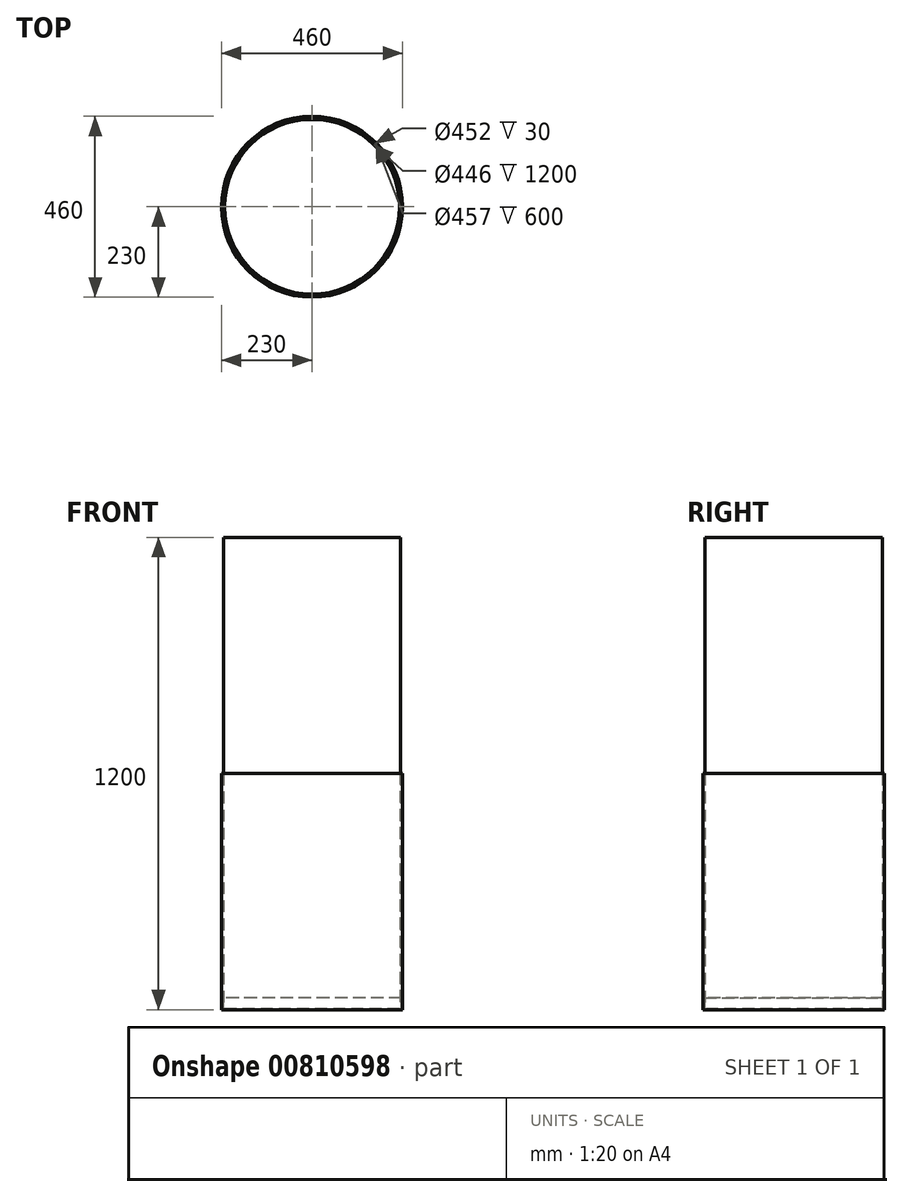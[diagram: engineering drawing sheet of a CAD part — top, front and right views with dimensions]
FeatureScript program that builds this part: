
annotation { "Feature Type Name" : "Feature", "Feature Type Description" : "" }
export const myFeature = defineFeature(function(context is Context, id is Id, definition is map)
    precondition{}
    {
        {
            var Q0;
            Q0=qCreatedBy(makeId("Top.planeOp"),FACE);
            var sketch = newSketch(context, id + "F0", { "sketchPlane" : qUnion([Q0])});
            skCircle(sketch, "E0", {"center": v(0, 0) * mm, "radius": 230 * mm});
            skCircle(sketch, "E1.0", {"center": v(0, 0) * mm, "radius": 228.5 * mm});
            skSolve(sketch);
        }
        {
            var Q0;
            Q0=makeQuery(id+"F0.imprint","IMPRINT",FACE,{"disambiguationData":[TD([[makeQuery(id+"F0.imprint","IMPRINT",EDGE,{"derivedFrom":sQuery(id+"F0.wireOp",EDGE,"E0")}),1.0]])]});
            extrude(context, id + "F1", {"entities" : qUnion([Q0]), "depth" : 600 * mm, "offsetDistance" : 25 * mm});
        }
        {
            var Q0;
            Q0=qCreatedBy(makeId("Top.planeOp"),FACE);
            var sketch = newSketch(context, id + "F2", { "sketchPlane" : qUnion([Q0])});
            skCircle(sketch, "E2", {"center": v(0, 0) * mm, "radius": 222 * mm});
            skSolve(sketch);
        }
        {
            var Q0;
            Q0=makeQuery(id+"F2.imprint","IMPRINT",FACE,{"disambiguationData":[TD([[makeQuery(id+"F2.imprint","IMPRINT",EDGE,{"derivedFrom":sQuery(id+"F2.wireOp",EDGE,"E2")}),1.0]])]});
            extrude(context, id + "F3", {"entities" : qUnion([Q0]), "depth" : 2 * mm, "offsetDistance" : 25 * mm});
        }
        {
            var Q0;
            Q0=qCreatedBy(makeId("Top.planeOp"),FACE);
            var sketch = newSketch(context, id + "F4", { "sketchPlane" : qUnion([Q0])});
            skCircle(sketch, "E3", {"center": v(0, 0) * mm, "radius": 228 * mm});
            skCircle(sketch, "E4.0", {"center": v(0, 0) * mm, "radius": 233 * mm});
            skCircle(sketch, "E5.0", {"center": v(0, 0) * mm, "radius": 226 * mm});
            skSolve(sketch);
        }
        {
            var Q0;
            Q0=makeQuery(id+"F4.imprint","IMPRINT",FACE,{"disambiguationData":[TD([[makeQuery(id+"F4.imprint","IMPRINT",EDGE,{"derivedFrom":sQuery(id+"F4.wireOp",EDGE,"E3")}),1.0]])]});
            extrude(context, id + "F5", {"entities" : qUnion([Q0]), "depth" : 30 * mm, "offsetDistance" : 25 * mm});
        }
        {
            var Q0;
            Q0=qCreatedBy(makeId("Top.planeOp"),FACE);
            var sketch = newSketch(context, id + "F6", { "sketchPlane" : qUnion([Q0])});
            skCircle(sketch, "E6", {"center": v(0, 0) * mm, "radius": 225 * mm});
            skCircle(sketch, "E7.0", {"center": v(0, 0) * mm, "radius": 223 * mm});
            skSolve(sketch);
        }
        {
            var Q0;
            Q0=makeQuery(id+"F6.imprint","IMPRINT",FACE,{"disambiguationData":[TD([[makeQuery(id+"F6.imprint","IMPRINT",EDGE,{"derivedFrom":sQuery(id+"F6.wireOp",EDGE,"E6")}),1.0]])]});
            extrude(context, id + "F7", {"entities" : qUnion([Q0]), "depth" : 1200 * mm, "offsetDistance" : 25 * mm});
        }
    });
